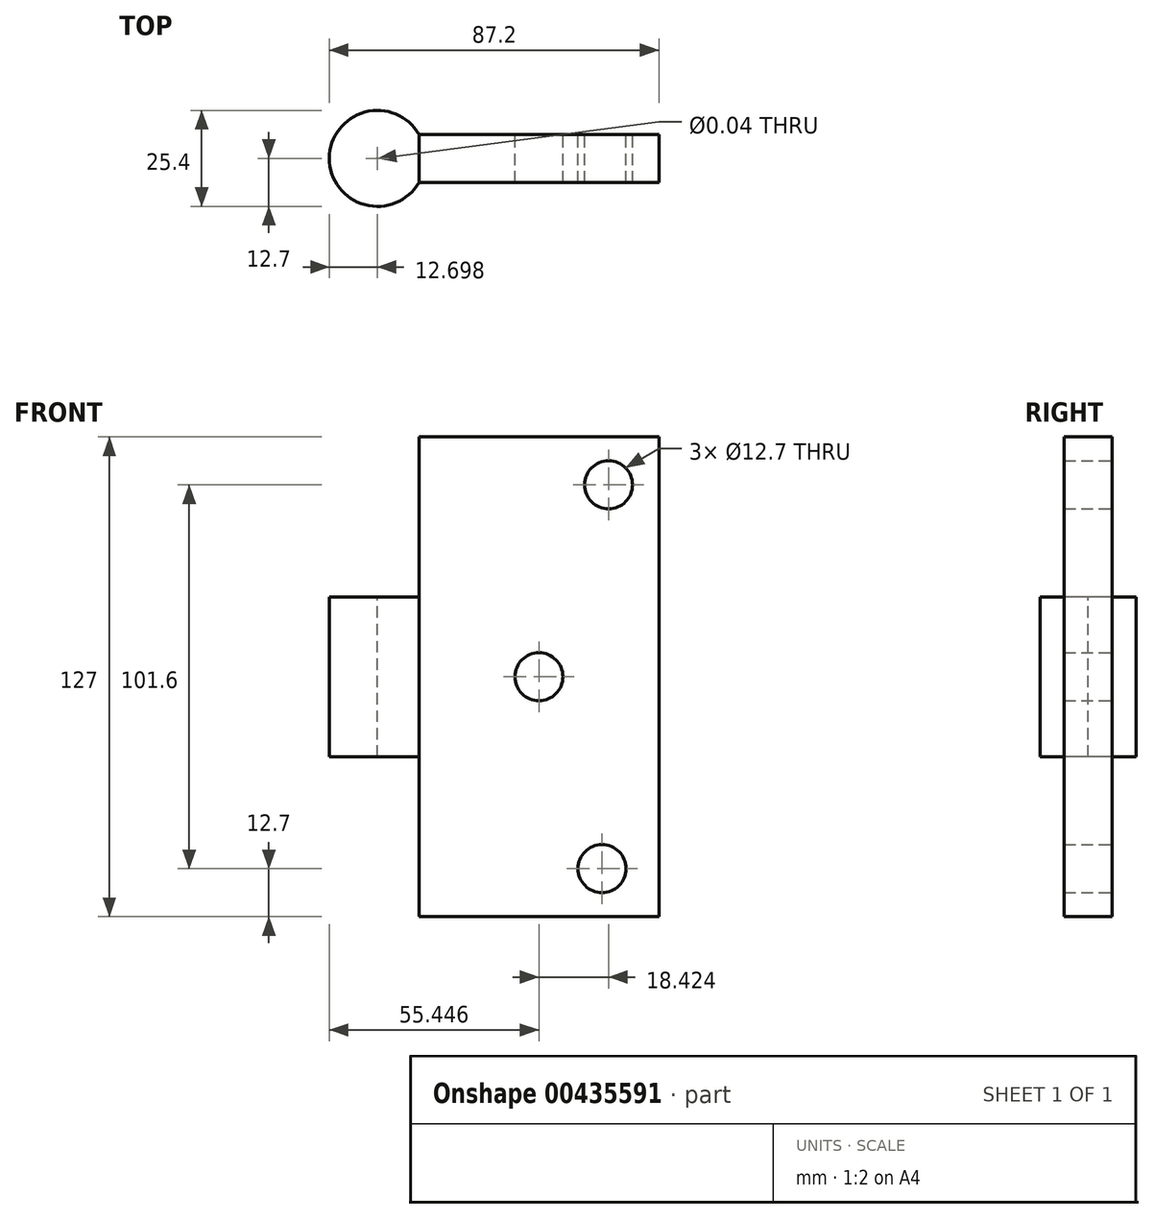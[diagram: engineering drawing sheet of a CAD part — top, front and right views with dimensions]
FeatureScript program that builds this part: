
annotation { "Feature Type Name" : "Feature", "Feature Type Description" : "" }
export const myFeature = defineFeature(function(context is Context, id is Id, definition is map)
    precondition{}
    {
        {
            var Q0;
            Q0=qCreatedBy(makeId("Top.planeOp"),FACE);
            var sketch = newSketch(context, id + "F0", { "sketchPlane" : qUnion([Q0])});
            skLineSegment(sketch, "E0.bottom", {"start": v(-31.75, 6.35) * mm, "end": v(31.75, 6.35) * mm});
            skLineSegment(sketch, "E0.top", {"start": v(-31.75, -6.35) * mm, "end": v(31.75, -6.35) * mm});
            skLineSegment(sketch, "E0.left", {"start": v(-31.75, 6.35) * mm, "end": v(-31.75, -6.35) * mm});
            skPoint(sketch, "E0.middle", {"position": v(0, 0) * mm});
            skCircle(sketch, "E1", {"center": v(42.75, 0) * mm, "radius": 12.7 * mm});
            skLineSegment(sketch, "E2", {"start": v(31.75, 6.35) * mm, "end": v(31.75, -6.35) * mm});
            skSolve(sketch);
        }
        {
            var Q0;
            Q0 = qSketchRegion(id + "F0", true);
            var Q1;
            Q1=sQuery(id+"F0.wireOp",EDGE,"E1");
            extrude(context, id + "F1", {"entities" : qUnion([Q0]), "surfaceEntities" : qUnion([Q1]), "oppositeDirection" : true, "depth" : 127 * mm});
        }
        {
            var Q0;
            Q0=makeQuery(id+"F1.opExtrude","SWEPT_FACE",FACE,{"disambiguationData":[OSD([sQuery(id+"F0.wireOp",EDGE,"E0.top")])]});
            var sketch = newSketch(context, id + "F2", { "sketchPlane" : qUnion([Q0])});
            skLineSegment(sketch, "E3.bottom", {"start": v(31.75, 0) * mm, "end": v(61.28, 0) * mm});
            skLineSegment(sketch, "E3.top", {"start": v(31.75, -42.34) * mm, "end": v(61.28, -42.34) * mm});
            skLineSegment(sketch, "E3.left", {"start": v(31.75, 0) * mm, "end": v(31.75, -42.34) * mm});
            skLineSegment(sketch, "E3.right", {"start": v(61.28, 0) * mm, "end": v(61.28, -42.34) * mm});
            skLineSegment(sketch, "E4.bottom", {"start": v(31.75, -127) * mm, "end": v(61.28, -127) * mm});
            skLineSegment(sketch, "E4.top", {"start": v(31.75, -84.66) * mm, "end": v(61.28, -84.66) * mm});
            skLineSegment(sketch, "E4.left", {"start": v(31.75, -127) * mm, "end": v(31.75, -84.66) * mm});
            skLineSegment(sketch, "E4.right", {"start": v(61.28, -127) * mm, "end": v(61.28, -84.66) * mm});
            skSolve(sketch);
        }
        {
            var Q0;
            Q0=makeQuery(id+"F2.imprint","IMPRINT",FACE,{"disambiguationData":[TD([[makeQuery(id+"F2.imprint","IMPRINT",EDGE,{"derivedFrom":sQuery(id+"F2.wireOp",EDGE,"E3.bottom")}),-1.0]])]});
            var Q1;
            Q1=makeQuery(id+"F2.imprint","IMPRINT",FACE,{"disambiguationData":[TD([[makeQuery(id+"F2.imprint","IMPRINT",EDGE,{"derivedFrom":sQuery(id+"F2.wireOp",EDGE,"E4.bottom")}),1.0]])]});
            extrude(context, id + "F3", {"entities" : qUnion([Q0, Q1]), "operationType" : NewBodyOperationType.REMOVE, "depth" : 25.4 * mm, "hasSecondDirection" : true, "secondDirectionOppositeDirection" : true, "secondDirectionDepth" : 25.4 * mm});
        }
        {
            var Q0;
            Q0=makeQuery(id+"F1.opExtrude","SWEPT_FACE",FACE,{"disambiguationData":[OSD([sQuery(id+"F0.wireOp",EDGE,"E0.top")])]});
            var sketch = newSketch(context, id + "F4", { "sketchPlane" : qUnion([Q0])});
            skCircle(sketch, "E5", {"center": v(-18.42, -12.7) * mm, "radius": 6.35 * mm});
            skCircle(sketch, "E6", {"center": v(0, -63.5) * mm, "radius": 6.35 * mm});
            skCircle(sketch, "E7", {"center": v(-16.7, -114.3) * mm, "radius": 6.35 * mm});
            skSolve(sketch);
        }
        {
            var Q0;
            Q0=sQuery(id+"F4.wireOp",VERTEX,"E5.center");
            var Q1;
            Q1=sQuery(id+"F4.wireOp",VERTEX,"E7.center");
            var Q2;
            Q2=sQuery(id+"F4.wireOp",VERTEX,"E6.center");
            var Q3;
            Q3=makeQuery(id+"F1.opExtrude","SWEPT_BODY",BODY,{"disambiguationData":[OSD([sQuery(id+"F0.wireOp",EDGE,"E0.bottom"),sQuery(id+"F0.wireOp",EDGE,"E0.top"),sQuery(id+"F0.wireOp",EDGE,"E0.left"),sQuery(id+"F0.wireOp",EDGE,"E1")])]});
            hole(context, id + "F5", {"style" : HoleStyle.SIMPLE, "endStyle" : HoleEndStyle.THROUGH, "holeDiameter" : 12.7 * mm, "isTappedThrough" : true, "tappedDepth" : 12.7 * mm, "tapClearance" : 3, "startFromSketch" : true, "locations" : qUnion([Q0, Q1, Q2]), "scope" : qUnion([Q3])});
        }
        {
            var Q0;
            Q0=sQuery(id+"F0.wireOp",VERTEX,"E1.center");
            var Q1;
            Q1=makeQuery(id+"F1.opExtrude","SWEPT_BODY",BODY,{"disambiguationData":[OSD([sQuery(id+"F0.wireOp",EDGE,"E0.bottom"),sQuery(id+"F0.wireOp",EDGE,"E0.top"),sQuery(id+"F0.wireOp",EDGE,"E0.left"),sQuery(id+"F0.wireOp",EDGE,"E1")])]});
            hole(context, id + "F6", {"style" : HoleStyle.SIMPLE, "endStyle" : HoleEndStyle.THROUGH, "holeDiameter" : 15 / 406.4 * mm, "isTappedThrough" : true, "tappedDepth" : 12.7 * mm, "tapClearance" : 3, "startFromSketch" : true, "locations" : qUnion([Q0]), "scope" : qUnion([Q1])});
        }
        {
            var Q0;
            Q0=makeQuery(id+"F1.opExtrude","SWEPT_BODY",BODY,{"disambiguationData":[OSD([sQuery(id+"F0.wireOp",EDGE,"E0.bottom"),sQuery(id+"F0.wireOp",EDGE,"E0.top"),sQuery(id+"F0.wireOp",EDGE,"E0.left"),sQuery(id+"F0.wireOp",EDGE,"E1")])]});
            var Q1;
            Q1=sQuery(id+"F0.wireOp",EDGE,"E1");
            transform(context, id + "F7", {"entities" : qUnion([Q0]), "transformType" : TransformType.ROTATION, "transformAxis" : qUnion([Q1]), "angle" : 180 * degree, "oppositeDirection" : true, "makeCopy" : false});
        }
    });
